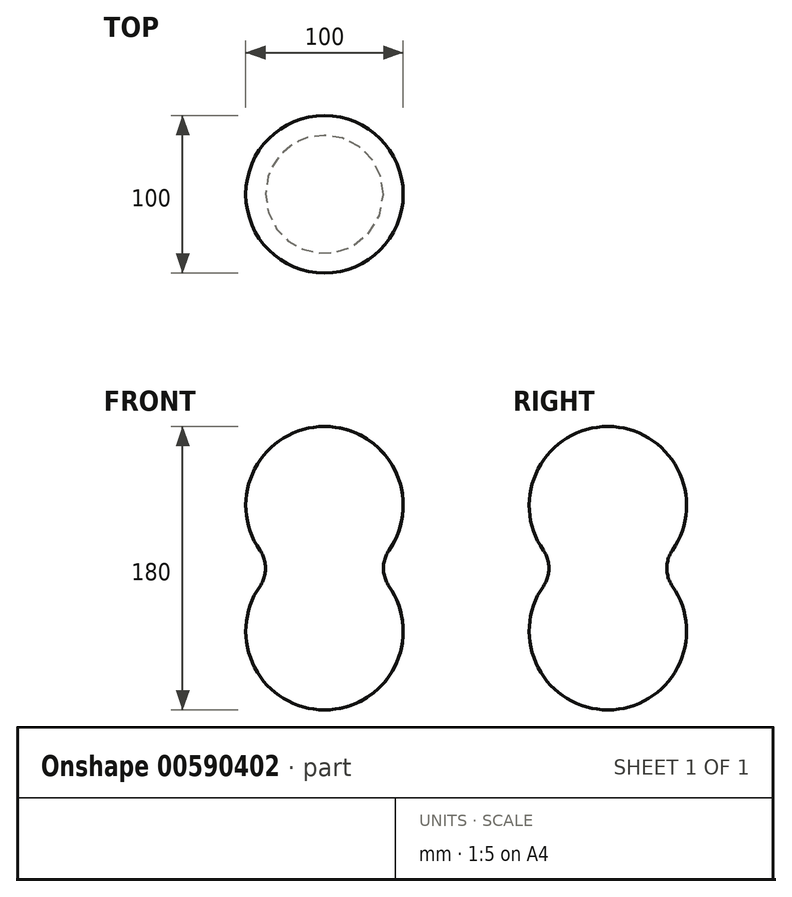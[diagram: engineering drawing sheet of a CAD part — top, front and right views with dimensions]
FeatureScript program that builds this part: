
annotation { "Feature Type Name" : "Feature", "Feature Type Description" : "" }
export const myFeature = defineFeature(function(context is Context, id is Id, definition is map)
    precondition{}
    {
        {
            var Q0;
            Q0=qCreatedBy(makeId("Front.planeOp"),FACE);
            var sketch = newSketch(context, id + "F0", { "sketchPlane" : qUnion([Q0])});
            skArc(sketch, "E0", {"start": v(0, 50) * mm, "mid": v(-50, 0) * mm, "end": v(0, -50) * mm});
            skLineSegment(sketch, "E1", {"start": v(0, 50) * mm, "end": v(0, -50) * mm});
            skSolve(sketch);
        }
        {
            var Q0;
            Q0 = qSketchRegion(id + "F0", true);
            var Q1;
            Q1=sQuery(id+"F0.wireOp",EDGE,"E1");
            revolve(context, id + "F1", {"entities" : qUnion([Q0]), "axis" : qUnion([Q1]), "revolveType" : RevolveType.FULL});
        }
        {
            var Q0;
            Q0=qCreatedBy(makeId("Top.planeOp"),FACE);
            cPlane(context, id + "F2", {"entities" : qUnion([Q0]), "cplaneType" : CPlaneType.OFFSET, "offset" : 40 * mm, "width" : 152.4 * mm, "height" : 152.4 * mm});
        }
        {
            var Q0;
            Q0=makeQuery(id+"F1.opRevolve","SWEPT_BODY",BODY,{"disambiguationData":[OSD([sQuery(id+"F0.wireOp",EDGE,"E0"),sQuery(id+"F0.wireOp",EDGE,"E1")])]});
            var Q1;
            Q1=qCreatedBy(id+"F2.planeOp",FACE);
            mirror(context, id + "F3", {"operationType" : NewBodyOperationType.ADD, "entities" : qUnion([Q0]), "mirrorPlane" : qUnion([Q1])});
        }
        {
            var Q0;
            Q0=makeQuery(id+"F1.opRevolve","SWEPT_FACE",FACE,{"disambiguationData":[OSD([sQuery(id+"F0.wireOp",EDGE,"E0")])]});
            fillet(context, id + "F4", {"entities" : qUnion([Q0]), "radius" : 20 * mm, "tangentPropagation" : true, "allowEdgeOverflow" : false});
        }
    });
